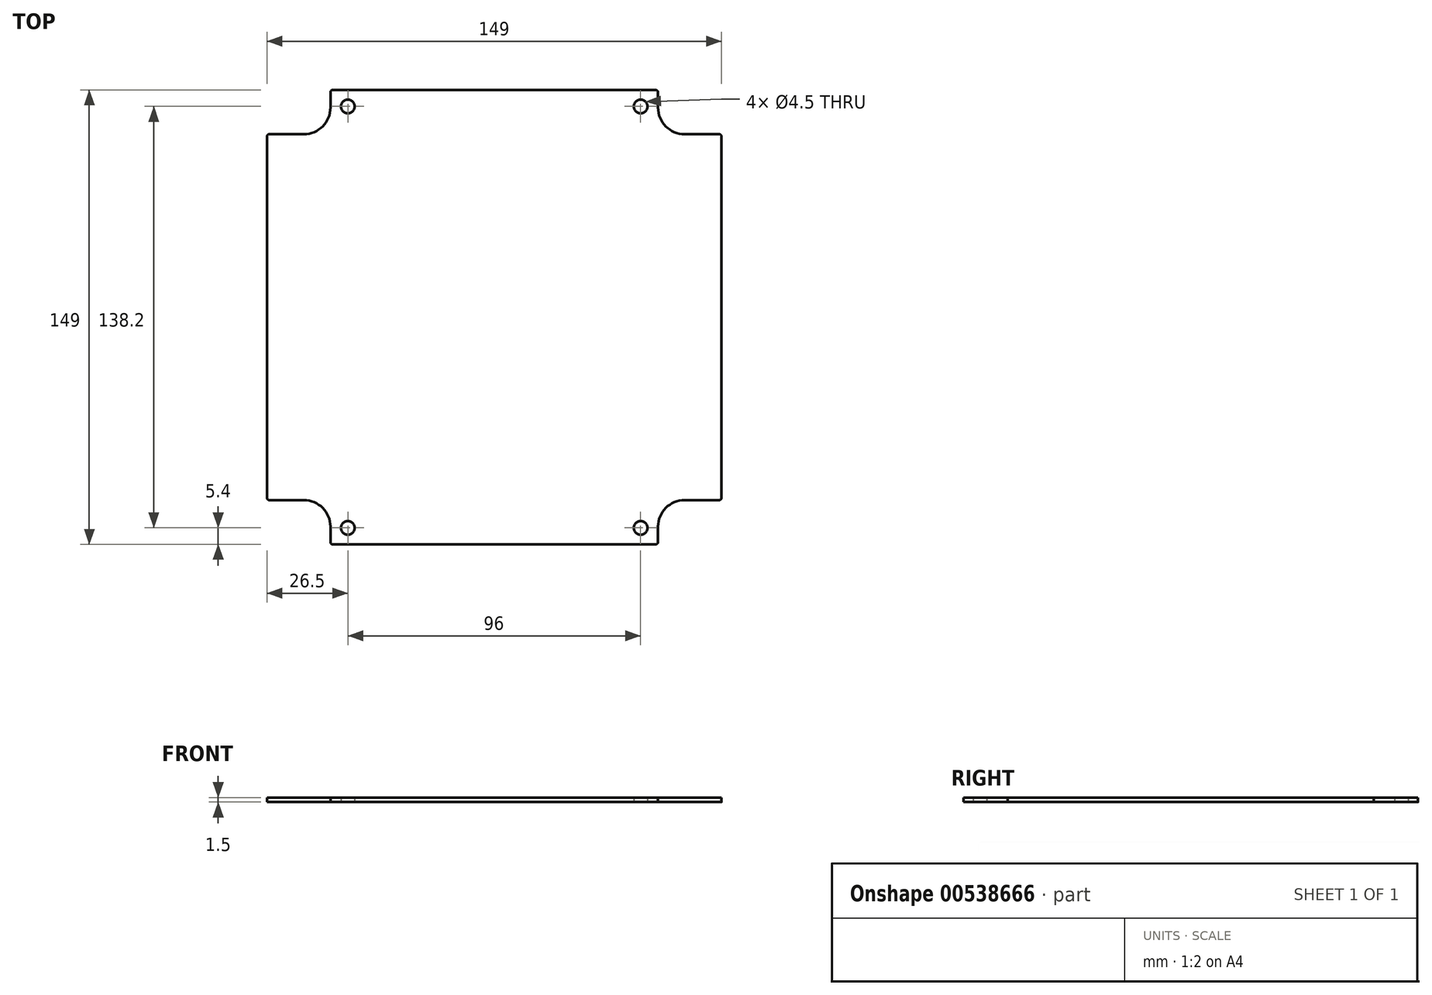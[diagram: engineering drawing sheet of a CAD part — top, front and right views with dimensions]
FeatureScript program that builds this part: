
annotation { "Feature Type Name" : "Feature", "Feature Type Description" : "" }
export const myFeature = defineFeature(function(context is Context, id is Id, definition is map)
    precondition{}
    {
        {
            var Q0;
            Q0=qCreatedBy(makeId("Top.planeOp"),FACE);
            var sketch = newSketch(context, id + "F0", { "sketchPlane" : qUnion([Q0])});
            skLineSegment(sketch, "E0.bottom", {"start": v(-52.9, 74.5) * mm, "end": v(52.9, 74.5) * mm});
            skLineSegment(sketch, "E0.left", {"start": v(-74.5, 59.2) * mm, "end": v(-74.5, -59.2) * mm});
            skPoint(sketch, "E0.middle", {"position": v(0, 0) * mm});
            skLineSegment(sketch, "E1", {"start": v(-73.7, -60) * mm, "end": v(-62.4, -60) * mm});
            skLineSegment(sketch, "E2", {"start": v(-53.7, -68.7) * mm, "end": v(-53.7, -73.7) * mm});
            skPoint(sketch, "E3.visualSharp", {"position": v(-53.7, -60) * mm});
            skArc(sketch, "E3.filletArc", {"start": v(-53.7, -68.7) * mm, "mid": v(-56.25, -62.55) * mm, "end": v(-62.4, -60) * mm});
            skPoint(sketch, "E4.orphan", {"position": v(-74.5, -74.5) * mm});
            skLineSegment(sketch, "E5.MirrorCS", {"start": v(53.7, -68.7) * mm, "end": v(53.7, -73.7) * mm});
            skPoint(sketch, "E6.MirrorP", {"position": v(53.7, -60) * mm});
            skLineSegment(sketch, "E7.MirrorCS", {"start": v(52.9, -74.5) * mm, "end": v(-52.9, -74.5) * mm});
            skArc(sketch, "E8.MirrorCS", {"start": v(53.7, -68.7) * mm, "mid": v(56.25, -62.55) * mm, "end": v(62.4, -60) * mm});
            skPoint(sketch, "E9.MirrorP", {"position": v(74.5, -74.5) * mm});
            skLineSegment(sketch, "E10.MirrorCS", {"start": v(73.7, -60) * mm, "end": v(62.4, -60) * mm});
            skLineSegment(sketch, "E11.MirrorCS", {"start": v(74.5, 59.2) * mm, "end": v(74.5, -59.2) * mm});
            skLineSegment(sketch, "E12.MirrorCS", {"start": v(74.5, -59.2) * mm, "end": v(74.5, 59.2) * mm});
            skLineSegment(sketch, "E13.MirrorCS", {"start": v(53.7, 68.7) * mm, "end": v(53.7, 73.7) * mm});
            skLineSegment(sketch, "E14.MirrorCS", {"start": v(-74.5, -59.2) * mm, "end": v(-74.5, 59.2) * mm});
            skLineSegment(sketch, "E15.MirrorCS", {"start": v(-53.7, 68.7) * mm, "end": v(-53.7, 73.7) * mm});
            skArc(sketch, "E16.MirrorCS", {"start": v(53.7, 68.7) * mm, "mid": v(56.25, 62.55) * mm, "end": v(62.4, 60) * mm});
            skArc(sketch, "E17.MirrorCS", {"start": v(-53.7, 68.7) * mm, "mid": v(-56.25, 62.55) * mm, "end": v(-62.4, 60) * mm});
            skPoint(sketch, "E18.MirrorP", {"position": v(-53.7, 60) * mm});
            skPoint(sketch, "E19.MirrorP", {"position": v(-74.5, 74.5) * mm});
            skPoint(sketch, "E20.MirrorP", {"position": v(53.7, 60) * mm});
            skLineSegment(sketch, "E21.MirrorCS", {"start": v(73.7, 60) * mm, "end": v(62.4, 60) * mm});
            skLineSegment(sketch, "E22.MirrorCS", {"start": v(52.9, 74.5) * mm, "end": v(-52.9, 74.5) * mm});
            skPoint(sketch, "E23.MirrorP", {"position": v(74.5, 74.5) * mm});
            skLineSegment(sketch, "E24.MirrorCS", {"start": v(-73.7, 60) * mm, "end": v(-62.4, 60) * mm});
            skCircle(sketch, "E25", {"center": v(-48, -69.1) * mm, "radius": 2.25 * mm});
            skCircle(sketch, "E26.MirrorC", {"center": v(48, -69.1) * mm, "radius": 2.25 * mm});
            skCircle(sketch, "E27.MirrorC", {"center": v(-48, 69.1) * mm, "radius": 2.25 * mm});
            skCircle(sketch, "E28.MirrorC", {"center": v(48, 69.1) * mm, "radius": 2.25 * mm});
            skPoint(sketch, "E29.visualSharp", {"position": v(74.5, 60) * mm});
            skArc(sketch, "E29.filletArc", {"start": v(74.5, 59.2) * mm, "mid": v(74.27, 59.77) * mm, "end": v(73.7, 60) * mm});
            skPoint(sketch, "E30.visualSharp", {"position": v(53.7, 74.5) * mm});
            skArc(sketch, "E30.filletArc", {"start": v(53.7, 73.7) * mm, "mid": v(53.47, 74.27) * mm, "end": v(52.9, 74.5) * mm});
            skPoint(sketch, "E31.visualSharp", {"position": v(-53.7, 74.5) * mm});
            skArc(sketch, "E31.filletArc", {"start": v(-52.9, 74.5) * mm, "mid": v(-53.47, 74.27) * mm, "end": v(-53.7, 73.7) * mm});
            skPoint(sketch, "E32.visualSharp", {"position": v(-74.5, 60) * mm});
            skArc(sketch, "E32.filletArc", {"start": v(-73.7, 60) * mm, "mid": v(-74.27, 59.77) * mm, "end": v(-74.5, 59.2) * mm});
            skPoint(sketch, "E33.visualSharp", {"position": v(-74.5, -60) * mm});
            skArc(sketch, "E33.filletArc", {"start": v(-74.5, -59.2) * mm, "mid": v(-74.27, -59.77) * mm, "end": v(-73.7, -60) * mm});
            skPoint(sketch, "E34.visualSharp", {"position": v(-53.7, -74.5) * mm});
            skArc(sketch, "E34.filletArc", {"start": v(-53.7, -73.7) * mm, "mid": v(-53.47, -74.27) * mm, "end": v(-52.9, -74.5) * mm});
            skPoint(sketch, "E35.visualSharp", {"position": v(53.7, -74.5) * mm});
            skArc(sketch, "E35.filletArc", {"start": v(52.9, -74.5) * mm, "mid": v(53.47, -74.27) * mm, "end": v(53.7, -73.7) * mm});
            skPoint(sketch, "E36.visualSharp", {"position": v(74.5, -60) * mm});
            skArc(sketch, "E36.filletArc", {"start": v(73.7, -60) * mm, "mid": v(74.27, -59.77) * mm, "end": v(74.5, -59.2) * mm});
            skSolve(sketch);
        }
        {
            var Q0;
            Q0 = qSketchRegion(id + "F0", true);
            extrude(context, id + "F1", {"entities" : qUnion([Q0]), "depth" : 1.5 * mm, "offsetDistance" : 25 * mm});
        }
    });
